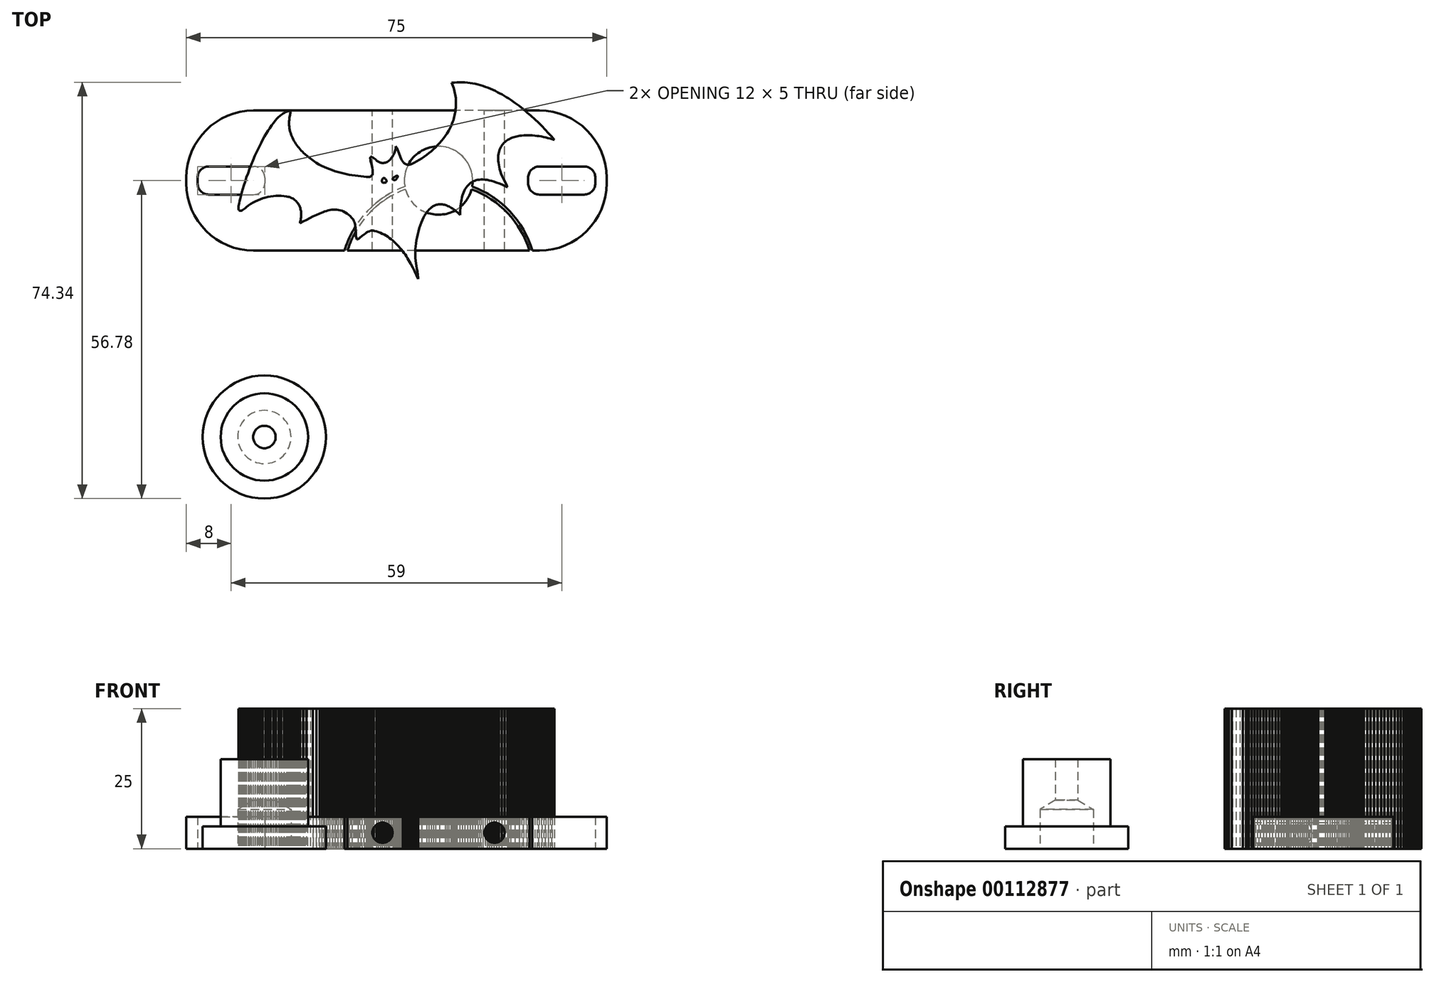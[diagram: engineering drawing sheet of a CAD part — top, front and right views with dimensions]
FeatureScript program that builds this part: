
annotation { "Feature Type Name" : "Feature", "Feature Type Description" : "" }
export const myFeature = defineFeature(function(context is Context, id is Id, definition is map)
    precondition{}
    {
        {
            var Q0;
            Q0=qCreatedBy(makeId("Top.planeOp"),FACE);
            var sketch = newSketch(context, id + "F0", { "sketchPlane" : qUnion([Q0])});
            skLineSegment(sketch, "E0.bottom", {"start": v(37.5, 12.5) * mm, "end": v(-37.5, 12.5) * mm});
            skLineSegment(sketch, "E0.top", {"start": v(37.5, -12.5) * mm, "end": v(24.27, -12.5) * mm});
            skLineSegment(sketch, "E0.left", {"start": v(37.5, 12.5) * mm, "end": v(37.5, -12.5) * mm});
            skLineSegment(sketch, "E0.right", {"start": v(-37.5, 12.5) * mm, "end": v(-37.5, -12.5) * mm});
            skPoint(sketch, "E0.middle", {"position": v(0, 0) * mm});
            skLineSegment(sketch, "E1", {"start": v(7.5, 12.5) * mm, "end": v(7.5, -12.5) * mm, "construction": true});
            skPoint(sketch, "E2", {"position": v(7.5, 0) * mm});
            skCircle(sketch, "E3", {"center": v(7.5, -17.5) * mm, "radius": 17.5 * mm});
            skCircle(sketch, "E4", {"center": v(7.5, -17.5) * mm, "radius": 17 * mm});
            skLineSegment(sketch, "E5.trimOffspring", {"start": v(-9.27, -12.5) * mm, "end": v(-37.5, -12.5) * mm});
            skLineSegment(sketch, "E6.trimOffspring", {"start": v(23.75, -12.5) * mm, "end": v(-8.75, -12.5) * mm});
            skLineSegment(sketch, "E7.bottom", {"start": v(35.5, 2.5) * mm, "end": v(23.5, 2.5) * mm});
            skLineSegment(sketch, "E7.top", {"start": v(35.5, -2.5) * mm, "end": v(23.5, -2.5) * mm});
            skLineSegment(sketch, "E7.left", {"start": v(35.5, 2.5) * mm, "end": v(35.5, -2.5) * mm});
            skLineSegment(sketch, "E7.right", {"start": v(23.5, 2.5) * mm, "end": v(23.5, -2.5) * mm});
            skPoint(sketch, "E7.middle", {"position": v(29.5, 0) * mm});
            skLineSegment(sketch, "E8.MirrorCS", {"start": v(-35.5, 2.5) * mm, "end": v(-23.5, 2.5) * mm});
            skLineSegment(sketch, "E9.MirrorCS", {"start": v(-23.5, 2.5) * mm, "end": v(-23.5, -2.5) * mm});
            skLineSegment(sketch, "E10.MirrorCS", {"start": v(-35.5, -2.5) * mm, "end": v(-23.5, -2.5) * mm});
            skLineSegment(sketch, "E11.MirrorCS", {"start": v(-35.5, 2.5) * mm, "end": v(-35.5, -2.5) * mm});
            skCircle(sketch, "E12", {"center": v(-23.58, -45.78) * mm, "radius": 11 * mm});
            skCircle(sketch, "E13", {"center": v(-23.58, -45.78) * mm, "radius": 7.8 * mm});
            skSolve(sketch);
        }
        {
            var Q0;
            Q0=makeQuery(id+"F0.imprint","IMPRINT",FACE,{"disambiguationData":[TD([[makeQuery(id+"F0.imprint","IMPRINT",EDGE,{"derivedFrom":sQuery(id+"F0.wireOp",EDGE,"E0.bottom")}),1.0]])]});
            extrude(context, id + "F1", {"entities" : qUnion([Q0]), "depth" : 5.7 * mm});
        }
        {
            var Q0;
            {var subQ0=sQuery(id+"F0.wireOp",EDGE,"E6.trimOffspring");Q0=makeQuery(id+"F0.imprint","IMPRINT",FACE,{"disambiguationData":[TD([[makeQuery(id+"F0.imprint","IMPRINT",EDGE,{"derivedFrom":subQ0}),-1.0]])]});}
            extrude(context, id + "F2", {"entities" : qUnion([Q0]), "depth" : 5.7 * mm});
        }
        {
            var Q0;
            Q0=makeQuery(id+"F1.opExtrude","SWEPT_FACE",FACE,{"disambiguationData":[OSD([sQuery(id+"F0.wireOp",EDGE,"E0.bottom")])]});
            var sketch = newSketch(context, id + "F3", { "sketchPlane" : qUnion([Q0])});
            skLineSegment(sketch, "E14", {"start": v(-7.5, 0) * mm, "end": v(-7.5, 5.7) * mm, "construction": true});
            skLineSegment(sketch, "E15", {"start": v(-37.5, 2.85) * mm, "end": v(37.5, 2.85) * mm, "construction": true});
            skPoint(sketch, "E16", {"position": v(2.5, 2.85) * mm});
            skPoint(sketch, "E17.MirrorP", {"position": v(-17.5, 2.85) * mm});
            skSolve(sketch);
        }
        {
            var Q0;
            Q0=sQuery(id+"F0.wireOp",VERTEX,"E2");
            var Q1;
            Q1=makeQuery(id+"F1.opExtrude","SWEPT_BODY",BODY,{"disambiguationData":[OSD([sQuery(id+"F0.wireOp",EDGE,"E0.bottom"),sQuery(id+"F0.wireOp",EDGE,"E0.top"),sQuery(id+"F0.wireOp",EDGE,"E0.left"),sQuery(id+"F0.wireOp",EDGE,"E0.right"),sQuery(id+"F0.wireOp",EDGE,"E3"),sQuery(id+"F0.wireOp",EDGE,"E5.trimOffspring"),sQuery(id+"F0.wireOp",EDGE,"E7.bottom"),sQuery(id+"F0.wireOp",EDGE,"E7.top"),sQuery(id+"F0.wireOp",EDGE,"E7.left"),sQuery(id+"F0.wireOp",EDGE,"E7.right"),sQuery(id+"F0.wireOp",EDGE,"E8.MirrorCS"),sQuery(id+"F0.wireOp",EDGE,"E9.MirrorCS"),sQuery(id+"F0.wireOp",EDGE,"E10.MirrorCS"),sQuery(id+"F0.wireOp",EDGE,"E11.MirrorCS")])]});
            var Q2;
            Q2=makeQuery(id+"F2.opExtrude","SWEPT_BODY",BODY,{"disambiguationData":[OSD([sQuery(id+"F0.wireOp",EDGE,"E4"),sQuery(id+"F0.wireOp",EDGE,"E6.trimOffspring")])]});
            hole(context, id + "F4", {"style" : HoleStyle.SIMPLE, "endStyle" : HoleEndStyle.THROUGH, "oppositeDirection" : true, "holeDiameter" : 12.2 * mm, "locations" : qUnion([Q0]), "scope" : qUnion([Q1, Q2]), "isTappedThrough" : true});
        }
        {
            var Q0;
            Q0=makeQuery(id+"F1.opExtrude","SWEPT_EDGE",EDGE,{"disambiguationData":[OSD([sQuery(id+"F0.wireOp",EDGE,"E0.bottom"),sQuery(id+"F0.wireOp",EDGE,"E0.right")])]});
            var Q1;
            Q1=makeQuery(id+"F1.opExtrude","SWEPT_EDGE",EDGE,{"disambiguationData":[OSD([sQuery(id+"F0.wireOp",EDGE,"E0.bottom"),sQuery(id+"F0.wireOp",EDGE,"E0.left")])]});
            var Q2;
            Q2=makeQuery(id+"F1.opExtrude","SWEPT_EDGE",EDGE,{"disambiguationData":[OSD([sQuery(id+"F0.wireOp",EDGE,"E0.right"),sQuery(id+"F0.wireOp",EDGE,"E5.trimOffspring")])]});
            var Q3;
            Q3=makeQuery(id+"F1.opExtrude","SWEPT_EDGE",EDGE,{"disambiguationData":[OSD([sQuery(id+"F0.wireOp",EDGE,"E0.top"),sQuery(id+"F0.wireOp",EDGE,"E0.left")])]});
            fillet(context, id + "F5", {"entities" : qUnion([Q0, Q1, Q2, Q3]), "radius" : 12 * mm, "tangentPropagation" : true, "allowEdgeOverflow" : false});
        }
        {
            var Q0;
            Q0=makeQuery(id+"F1.opExtrude","SWEPT_EDGE",EDGE,{"disambiguationData":[OSD([sQuery(id+"F0.wireOp",EDGE,"E7.bottom"),sQuery(id+"F0.wireOp",EDGE,"E7.right")])]});
            var Q1;
            Q1=makeQuery(id+"F1.opExtrude","SWEPT_EDGE",EDGE,{"disambiguationData":[OSD([sQuery(id+"F0.wireOp",EDGE,"E8.MirrorCS"),sQuery(id+"F0.wireOp",EDGE,"E11.MirrorCS")])]});
            var Q2;
            Q2=makeQuery(id+"F1.opExtrude","SWEPT_EDGE",EDGE,{"disambiguationData":[OSD([sQuery(id+"F0.wireOp",EDGE,"E8.MirrorCS"),sQuery(id+"F0.wireOp",EDGE,"E9.MirrorCS")])]});
            var Q3;
            Q3=makeQuery(id+"F1.opExtrude","SWEPT_EDGE",EDGE,{"disambiguationData":[OSD([sQuery(id+"F0.wireOp",EDGE,"E7.bottom"),sQuery(id+"F0.wireOp",EDGE,"E7.left")])]});
            var Q4;
            Q4=makeQuery(id+"F1.opExtrude","SWEPT_EDGE",EDGE,{"disambiguationData":[OSD([sQuery(id+"F0.wireOp",EDGE,"E7.top"),sQuery(id+"F0.wireOp",EDGE,"E7.left")])]});
            var Q5;
            Q5=makeQuery(id+"F1.opExtrude","SWEPT_EDGE",EDGE,{"disambiguationData":[OSD([sQuery(id+"F0.wireOp",EDGE,"E9.MirrorCS"),sQuery(id+"F0.wireOp",EDGE,"E10.MirrorCS")])]});
            var Q6;
            Q6=makeQuery(id+"F1.opExtrude","SWEPT_EDGE",EDGE,{"disambiguationData":[OSD([sQuery(id+"F0.wireOp",EDGE,"E10.MirrorCS"),sQuery(id+"F0.wireOp",EDGE,"E11.MirrorCS")])]});
            var Q7;
            Q7=makeQuery(id+"F1.opExtrude","SWEPT_EDGE",EDGE,{"disambiguationData":[OSD([sQuery(id+"F0.wireOp",EDGE,"E7.top"),sQuery(id+"F0.wireOp",EDGE,"E7.right")])]});
            fillet(context, id + "F6", {"entities" : qUnion([Q0, Q1, Q2, Q3, Q4, Q5, Q6, Q7]), "radius" : 2 * mm, "tangentPropagation" : true, "allowEdgeOverflow" : false});
        }
        {
            var Q0;
            Q0=sQuery(id+"F3.wireOp",VERTEX,"E17.MirrorP");
            var Q1;
            Q1=sQuery(id+"F3.wireOp",VERTEX,"E16");
            var Q2;
            Q2=makeQuery(id+"F1.opExtrude","SWEPT_BODY",BODY,{"disambiguationData":[OSD([sQuery(id+"F0.wireOp",EDGE,"E0.bottom"),sQuery(id+"F0.wireOp",EDGE,"E0.top"),sQuery(id+"F0.wireOp",EDGE,"E0.left"),sQuery(id+"F0.wireOp",EDGE,"E0.right"),sQuery(id+"F0.wireOp",EDGE,"E3"),sQuery(id+"F0.wireOp",EDGE,"E5.trimOffspring"),sQuery(id+"F0.wireOp",EDGE,"E7.bottom"),sQuery(id+"F0.wireOp",EDGE,"E7.top"),sQuery(id+"F0.wireOp",EDGE,"E7.left"),sQuery(id+"F0.wireOp",EDGE,"E7.right"),sQuery(id+"F0.wireOp",EDGE,"E8.MirrorCS"),sQuery(id+"F0.wireOp",EDGE,"E9.MirrorCS"),sQuery(id+"F0.wireOp",EDGE,"E10.MirrorCS"),sQuery(id+"F0.wireOp",EDGE,"E11.MirrorCS")])]});
            var Q3;
            Q3=makeQuery(id+"F2.opExtrude","SWEPT_BODY",BODY,{"disambiguationData":[OSD([sQuery(id+"F0.wireOp",EDGE,"E4"),sQuery(id+"F0.wireOp",EDGE,"E6.trimOffspring")])]});
            hole(context, id + "F7", {"style" : HoleStyle.SIMPLE, "endStyle" : HoleEndStyle.THROUGH, "holeDiameter" : 3.6 * mm, "locations" : qUnion([Q0, Q1]), "scope" : qUnion([Q2, Q3]), "isTappedThrough" : true});
        }
        {
            var Q0;
            Q0=makeQuery(id+"F0.imprint","IMPRINT",FACE,{"disambiguationData":[TD([[makeQuery(id+"F0.imprint","IMPRINT",EDGE,{"derivedFrom":sQuery(id+"F0.wireOp",EDGE,"E13")}),1.0]])]});
            extrude(context, id + "F8", {"entities" : qUnion([Q0]), "depth" : 16 * mm});
        }
        {
            var Q0;
            Q0=makeQuery(id+"F0.imprint","IMPRINT",FACE,{"disambiguationData":[TD([[makeQuery(id+"F0.imprint","IMPRINT",EDGE,{"derivedFrom":sQuery(id+"F0.wireOp",EDGE,"E12")}),1.0]])]});
            extrude(context, id + "F9", {"entities" : qUnion([Q0]), "operationType" : NewBodyOperationType.ADD, "depth" : 4 * mm});
        }
        {
            var Q0;
            Q0=sQuery(id+"F0.wireOp",VERTEX,"E12.center");
            var Q1;
            Q1=makeQuery(id+"F8.opExtrude","SWEPT_BODY",BODY,{"disambiguationData":[OSD([sQuery(id+"F0.wireOp",EDGE,"E13")])]});
            hole(context, id + "F10", {"style" : HoleStyle.SIMPLE, "endStyle" : HoleEndStyle.THROUGH, "oppositeDirection" : true, "holeDiameter" : 4 * mm, "locations" : qUnion([Q0]), "scope" : qUnion([Q1]), "isTappedThrough" : true});
        }
        {
            var Q0;
            Q0=sQuery(id+"F0.wireOp",VERTEX,"E12.center");
            var Q1;
            Q1=makeQuery(id+"F8.opExtrude","SWEPT_BODY",BODY,{"disambiguationData":[OSD([sQuery(id+"F0.wireOp",EDGE,"E13")])]});
            hole(context, id + "F11", {"style" : HoleStyle.SIMPLE, "endStyle" : HoleEndStyle.BLIND, "oppositeDirection" : true, "holeDiameter" : 9.5 * mm, "holeDepth" : 7 * mm, "locations" : qUnion([Q0]), "scope" : qUnion([Q1])});
        }
        {
            var Q0;
            Q0=qCreatedBy(makeId("Top.planeOp"),FACE);
            var sketch = newSketch(context, id + "F12", { "sketchPlane" : qUnion([Q0])});
            skLineSegment(sketch, "E18", {"start": v(3.84, -17.56) * mm, "end": v(3.55, -16.88) * mm});
            skLineSegment(sketch, "E19", {"start": v(3.55, -16.88) * mm, "end": v(3.24, -16.2) * mm});
            skLineSegment(sketch, "E20", {"start": v(3.24, -16.2) * mm, "end": v(2.9, -15.52) * mm});
            skLineSegment(sketch, "E21", {"start": v(2.9, -15.52) * mm, "end": v(2.56, -14.85) * mm});
            skLineSegment(sketch, "E22", {"start": v(2.56, -14.85) * mm, "end": v(2.18, -14.19) * mm});
            skLineSegment(sketch, "E23", {"start": v(2.18, -14.19) * mm, "end": v(1.98, -13.86) * mm});
            skLineSegment(sketch, "E24", {"start": v(1.98, -13.86) * mm, "end": v(1.78, -13.54) * mm});
            skLineSegment(sketch, "E25", {"start": v(1.78, -13.54) * mm, "end": v(1.57, -13.23) * mm});
            skLineSegment(sketch, "E26", {"start": v(1.57, -13.23) * mm, "end": v(1.35, -12.91) * mm});
            skLineSegment(sketch, "E27", {"start": v(1.35, -12.91) * mm, "end": v(1.12, -12.61) * mm});
            skLineSegment(sketch, "E28", {"start": v(1.12, -12.61) * mm, "end": v(0.9, -12.31) * mm});
            skLineSegment(sketch, "E29", {"start": v(0.9, -12.31) * mm, "end": v(0.65, -12.02) * mm});
            skLineSegment(sketch, "E30", {"start": v(0.65, -12.02) * mm, "end": v(0.4, -11.74) * mm});
            skLineSegment(sketch, "E31", {"start": v(0.4, -11.74) * mm, "end": v(0.15, -11.47) * mm});
            skLineSegment(sketch, "E32", {"start": v(0.15, -11.47) * mm, "end": v(-0.11, -11.2) * mm});
            skLineSegment(sketch, "E33", {"start": v(-0.11, -11.2) * mm, "end": v(-0.38, -10.95) * mm});
            skLineSegment(sketch, "E34", {"start": v(-0.38, -10.95) * mm, "end": v(-0.66, -10.7) * mm});
            skLineSegment(sketch, "E35", {"start": v(-0.66, -10.7) * mm, "end": v(-0.95, -10.47) * mm});
            skLineSegment(sketch, "E36", {"start": v(-0.95, -10.47) * mm, "end": v(-1.25, -10.25) * mm});
            skLineSegment(sketch, "E37", {"start": v(-1.25, -10.25) * mm, "end": v(-1.55, -10.04) * mm});
            skLineSegment(sketch, "E38", {"start": v(-1.55, -10.04) * mm, "end": v(-1.87, -9.85) * mm});
            skLineSegment(sketch, "E39", {"start": v(-1.87, -9.85) * mm, "end": v(-2.19, -9.67) * mm});
            skLineSegment(sketch, "E40", {"start": v(-2.19, -9.67) * mm, "end": v(-2.52, -9.5) * mm});
            skLineSegment(sketch, "E41", {"start": v(-2.52, -9.5) * mm, "end": v(-2.87, -9.35) * mm});
            skLineSegment(sketch, "E42", {"start": v(-2.87, -9.35) * mm, "end": v(-3.22, -9.2) * mm});
            skLineSegment(sketch, "E43", {"start": v(-3.22, -9.2) * mm, "end": v(-3.58, -9.09) * mm});
            skLineSegment(sketch, "E44", {"start": v(-3.58, -9.09) * mm, "end": v(-3.95, -8.98) * mm});
            skLineSegment(sketch, "E45", {"start": v(-3.95, -8.98) * mm, "end": v(-4.06, -8.95) * mm});
            skLineSegment(sketch, "E46", {"start": v(-4.06, -8.95) * mm, "end": v(-4.17, -8.93) * mm});
            skLineSegment(sketch, "E47", {"start": v(-4.17, -8.93) * mm, "end": v(-4.29, -8.93) * mm});
            skLineSegment(sketch, "E48", {"start": v(-4.29, -8.93) * mm, "end": v(-4.4, -8.93) * mm});
            skLineSegment(sketch, "E49", {"start": v(-4.4, -8.93) * mm, "end": v(-4.51, -8.95) * mm});
            skLineSegment(sketch, "E50", {"start": v(-4.51, -8.95) * mm, "end": v(-4.63, -8.97) * mm});
            skLineSegment(sketch, "E51", {"start": v(-4.63, -8.97) * mm, "end": v(-4.86, -9.05) * mm});
            skLineSegment(sketch, "E52", {"start": v(-4.86, -9.05) * mm, "end": v(-5.08, -9.15) * mm});
            skLineSegment(sketch, "E53", {"start": v(-5.08, -9.15) * mm, "end": v(-5.3, -9.28) * mm});
            skLineSegment(sketch, "E54", {"start": v(-5.3, -9.28) * mm, "end": v(-5.53, -9.43) * mm});
            skLineSegment(sketch, "E55", {"start": v(-5.53, -9.43) * mm, "end": v(-5.75, -9.58) * mm});
            skLineSegment(sketch, "E56", {"start": v(-5.75, -9.58) * mm, "end": v(-6.15, -9.9) * mm});
            skLineSegment(sketch, "E57", {"start": v(-6.15, -9.9) * mm, "end": v(-6.52, -10.2) * mm});
            skLineSegment(sketch, "E58", {"start": v(-6.52, -10.2) * mm, "end": v(-6.68, -10.33) * mm});
            skLineSegment(sketch, "E59", {"start": v(-6.68, -10.33) * mm, "end": v(-6.83, -10.43) * mm});
            skLineSegment(sketch, "E60", {"start": v(-6.83, -10.43) * mm, "end": v(-6.96, -10.5) * mm});
            skLineSegment(sketch, "E61", {"start": v(-6.96, -10.5) * mm, "end": v(-7.02, -10.53) * mm});
            skLineSegment(sketch, "E62", {"start": v(-7.02, -10.53) * mm, "end": v(-7.07, -10.54) * mm});
            skLineSegment(sketch, "E63", {"start": v(-7.07, -10.54) * mm, "end": v(-7.13, -10.34) * mm});
            skLineSegment(sketch, "E64", {"start": v(-7.13, -10.34) * mm, "end": v(-7.18, -10.14) * mm});
            skLineSegment(sketch, "E65", {"start": v(-7.18, -10.14) * mm, "end": v(-7.21, -9.93) * mm});
            skLineSegment(sketch, "E66", {"start": v(-7.21, -9.93) * mm, "end": v(-7.24, -9.72) * mm});
            skLineSegment(sketch, "E67", {"start": v(-7.24, -9.72) * mm, "end": v(-7.27, -9.27) * mm});
            skLineSegment(sketch, "E68", {"start": v(-7.27, -9.27) * mm, "end": v(-7.29, -8.82) * mm});
            skLineSegment(sketch, "E69", {"start": v(-7.29, -8.82) * mm, "end": v(-7.33, -8.35) * mm});
            skLineSegment(sketch, "E70", {"start": v(-7.33, -8.35) * mm, "end": v(-7.35, -8.12) * mm});
            skLineSegment(sketch, "E71", {"start": v(-7.35, -8.12) * mm, "end": v(-7.4, -7.89) * mm});
            skLineSegment(sketch, "E72", {"start": v(-7.4, -7.89) * mm, "end": v(-7.45, -7.66) * mm});
            skLineSegment(sketch, "E73", {"start": v(-7.45, -7.66) * mm, "end": v(-7.52, -7.43) * mm});
            skLineSegment(sketch, "E74", {"start": v(-7.52, -7.43) * mm, "end": v(-7.6, -7.2) * mm});
            skLineSegment(sketch, "E75", {"start": v(-7.6, -7.2) * mm, "end": v(-7.72, -6.98) * mm});
            skLineSegment(sketch, "E76", {"start": v(-7.72, -6.98) * mm, "end": v(-8, -6.64) * mm});
            skLineSegment(sketch, "E77", {"start": v(-8, -6.64) * mm, "end": v(-8.28, -6.35) * mm});
            skLineSegment(sketch, "E78", {"start": v(-8.28, -6.35) * mm, "end": v(-8.56, -6.09) * mm});
            skLineSegment(sketch, "E79", {"start": v(-8.56, -6.09) * mm, "end": v(-8.85, -5.86) * mm});
            skLineSegment(sketch, "E80", {"start": v(-8.85, -5.86) * mm, "end": v(-9.14, -5.68) * mm});
            skLineSegment(sketch, "E81", {"start": v(-9.14, -5.68) * mm, "end": v(-9.44, -5.52) * mm});
            skLineSegment(sketch, "E82", {"start": v(-9.44, -5.52) * mm, "end": v(-9.74, -5.4) * mm});
            skLineSegment(sketch, "E83", {"start": v(-9.74, -5.4) * mm, "end": v(-10.04, -5.3) * mm});
            skLineSegment(sketch, "E84", {"start": v(-10.04, -5.3) * mm, "end": v(-10.34, -5.24) * mm});
            skLineSegment(sketch, "E85", {"start": v(-10.34, -5.24) * mm, "end": v(-10.64, -5.2) * mm});
            skLineSegment(sketch, "E86", {"start": v(-10.64, -5.2) * mm, "end": v(-10.95, -5.18) * mm});
            skLineSegment(sketch, "E87", {"start": v(-10.95, -5.18) * mm, "end": v(-11.26, -5.2) * mm});
            skLineSegment(sketch, "E88", {"start": v(-11.26, -5.2) * mm, "end": v(-11.57, -5.22) * mm});
            skLineSegment(sketch, "E89", {"start": v(-11.57, -5.22) * mm, "end": v(-11.88, -5.27) * mm});
            skLineSegment(sketch, "E90", {"start": v(-11.88, -5.27) * mm, "end": v(-12.19, -5.34) * mm});
            skLineSegment(sketch, "E91", {"start": v(-12.19, -5.34) * mm, "end": v(-12.5, -5.42) * mm});
            skLineSegment(sketch, "E92", {"start": v(-12.5, -5.42) * mm, "end": v(-12.8, -5.52) * mm});
            skLineSegment(sketch, "E93", {"start": v(-12.8, -5.52) * mm, "end": v(-13.1, -5.62) * mm});
            skLineSegment(sketch, "E94", {"start": v(-13.1, -5.62) * mm, "end": v(-13.4, -5.74) * mm});
            skLineSegment(sketch, "E95", {"start": v(-13.4, -5.74) * mm, "end": v(-13.7, -5.86) * mm});
            skLineSegment(sketch, "E96", {"start": v(-13.7, -5.86) * mm, "end": v(-14.3, -6.14) * mm});
            skLineSegment(sketch, "E97", {"start": v(-14.3, -6.14) * mm, "end": v(-14.9, -6.43) * mm});
            skLineSegment(sketch, "E98", {"start": v(-14.9, -6.43) * mm, "end": v(-16.08, -7.04) * mm});
            skLineSegment(sketch, "E99", {"start": v(-16.08, -7.04) * mm, "end": v(-16.66, -7.32) * mm});
            skLineSegment(sketch, "E100", {"start": v(-16.66, -7.32) * mm, "end": v(-17.24, -7.58) * mm});
            skLineSegment(sketch, "E101", {"start": v(-17.24, -7.58) * mm, "end": v(-17.19, -7.4) * mm});
            skLineSegment(sketch, "E102", {"start": v(-17.19, -7.4) * mm, "end": v(-17.14, -7.2) * mm});
            skLineSegment(sketch, "E103", {"start": v(-17.14, -7.2) * mm, "end": v(-17.1, -7) * mm});
            skLineSegment(sketch, "E104", {"start": v(-17.1, -7) * mm, "end": v(-17.06, -6.81) * mm});
            skLineSegment(sketch, "E105", {"start": v(-17.06, -6.81) * mm, "end": v(-17.04, -6.62) * mm});
            skLineSegment(sketch, "E106", {"start": v(-17.04, -6.62) * mm, "end": v(-17.02, -6.43) * mm});
            skLineSegment(sketch, "E107", {"start": v(-17.02, -6.43) * mm, "end": v(-17, -6.23) * mm});
            skLineSegment(sketch, "E108", {"start": v(-17, -6.23) * mm, "end": v(-17, -6.04) * mm});
            skLineSegment(sketch, "E109", {"start": v(-17, -6.04) * mm, "end": v(-17.01, -5.85) * mm});
            skLineSegment(sketch, "E110", {"start": v(-17.01, -5.85) * mm, "end": v(-17.03, -5.66) * mm});
            skLineSegment(sketch, "E111", {"start": v(-17.03, -5.66) * mm, "end": v(-17.05, -5.48) * mm});
            skLineSegment(sketch, "E112", {"start": v(-17.05, -5.48) * mm, "end": v(-17.08, -5.3) * mm});
            skLineSegment(sketch, "E113", {"start": v(-17.08, -5.3) * mm, "end": v(-17.12, -5.12) * mm});
            skLineSegment(sketch, "E114", {"start": v(-17.12, -5.12) * mm, "end": v(-17.17, -4.94) * mm});
            skLineSegment(sketch, "E115", {"start": v(-17.17, -4.94) * mm, "end": v(-17.23, -4.77) * mm});
            skLineSegment(sketch, "E116", {"start": v(-17.23, -4.77) * mm, "end": v(-17.3, -4.6) * mm});
            skLineSegment(sketch, "E117", {"start": v(-17.3, -4.6) * mm, "end": v(-17.37, -4.44) * mm});
            skLineSegment(sketch, "E118", {"start": v(-17.37, -4.44) * mm, "end": v(-17.45, -4.28) * mm});
            skLineSegment(sketch, "E119", {"start": v(-17.45, -4.28) * mm, "end": v(-17.54, -4.13) * mm});
            skLineSegment(sketch, "E120", {"start": v(-17.54, -4.13) * mm, "end": v(-17.64, -3.98) * mm});
            skLineSegment(sketch, "E121", {"start": v(-17.64, -3.98) * mm, "end": v(-17.75, -3.84) * mm});
            skLineSegment(sketch, "E122", {"start": v(-17.75, -3.84) * mm, "end": v(-17.87, -3.7) * mm});
            skLineSegment(sketch, "E123", {"start": v(-17.87, -3.7) * mm, "end": v(-18, -3.58) * mm});
            skLineSegment(sketch, "E124", {"start": v(-18, -3.58) * mm, "end": v(-18.14, -3.46) * mm});
            skLineSegment(sketch, "E125", {"start": v(-18.14, -3.46) * mm, "end": v(-18.29, -3.35) * mm});
            skLineSegment(sketch, "E126", {"start": v(-18.29, -3.35) * mm, "end": v(-18.45, -3.25) * mm});
            skLineSegment(sketch, "E127", {"start": v(-18.45, -3.25) * mm, "end": v(-18.61, -3.16) * mm});
            skLineSegment(sketch, "E128", {"start": v(-18.61, -3.16) * mm, "end": v(-18.79, -3.07) * mm});
            skLineSegment(sketch, "E129", {"start": v(-18.79, -3.07) * mm, "end": v(-18.98, -3) * mm});
            skLineSegment(sketch, "E130", {"start": v(-18.98, -3) * mm, "end": v(-19.17, -2.93) * mm});
            skLineSegment(sketch, "E131", {"start": v(-19.17, -2.93) * mm, "end": v(-19.38, -2.88) * mm});
            skLineSegment(sketch, "E132", {"start": v(-19.38, -2.88) * mm, "end": v(-19.6, -2.84) * mm});
            skLineSegment(sketch, "E133", {"start": v(-19.6, -2.84) * mm, "end": v(-20.07, -2.78) * mm});
            skLineSegment(sketch, "E134", {"start": v(-20.07, -2.78) * mm, "end": v(-20.55, -2.74) * mm});
            skLineSegment(sketch, "E135", {"start": v(-20.55, -2.74) * mm, "end": v(-21.03, -2.73) * mm});
            skLineSegment(sketch, "E136", {"start": v(-21.03, -2.73) * mm, "end": v(-21.5, -2.75) * mm});
            skLineSegment(sketch, "E137", {"start": v(-21.5, -2.75) * mm, "end": v(-21.98, -2.79) * mm});
            skLineSegment(sketch, "E138", {"start": v(-21.98, -2.79) * mm, "end": v(-22.46, -2.85) * mm});
            skLineSegment(sketch, "E139", {"start": v(-22.46, -2.85) * mm, "end": v(-22.93, -2.94) * mm});
            skLineSegment(sketch, "E140", {"start": v(-22.93, -2.94) * mm, "end": v(-23.4, -3.05) * mm});
            skLineSegment(sketch, "E141", {"start": v(-23.4, -3.05) * mm, "end": v(-23.85, -3.19) * mm});
            skLineSegment(sketch, "E142", {"start": v(-23.85, -3.19) * mm, "end": v(-24.3, -3.34) * mm});
            skLineSegment(sketch, "E143", {"start": v(-24.3, -3.34) * mm, "end": v(-24.75, -3.53) * mm});
            skLineSegment(sketch, "E144", {"start": v(-24.75, -3.53) * mm, "end": v(-25.18, -3.73) * mm});
            skLineSegment(sketch, "E145", {"start": v(-25.18, -3.73) * mm, "end": v(-25.6, -3.95) * mm});
            skLineSegment(sketch, "E146", {"start": v(-25.6, -3.95) * mm, "end": v(-26.02, -4.2) * mm});
            skLineSegment(sketch, "E147", {"start": v(-26.02, -4.2) * mm, "end": v(-26.42, -4.46) * mm});
            skLineSegment(sketch, "E148", {"start": v(-26.42, -4.46) * mm, "end": v(-26.8, -4.75) * mm});
            skLineSegment(sketch, "E149", {"start": v(-26.8, -4.75) * mm, "end": v(-27, -4.93) * mm});
            skLineSegment(sketch, "E150", {"start": v(-27, -4.93) * mm, "end": v(-27.2, -5.09) * mm});
            skLineSegment(sketch, "E151", {"start": v(-27.2, -5.09) * mm, "end": v(-27.37, -5.2) * mm});
            skLineSegment(sketch, "E152", {"start": v(-27.37, -5.2) * mm, "end": v(-27.54, -5.3) * mm});
            skLineSegment(sketch, "E153", {"start": v(-27.54, -5.3) * mm, "end": v(-27.68, -5.37) * mm});
            skLineSegment(sketch, "E154", {"start": v(-27.68, -5.37) * mm, "end": v(-27.81, -5.4) * mm});
            skLineSegment(sketch, "E155", {"start": v(-27.81, -5.4) * mm, "end": v(-27.93, -5.4) * mm});
            skLineSegment(sketch, "E156", {"start": v(-27.93, -5.4) * mm, "end": v(-27.98, -5.4) * mm});
            skLineSegment(sketch, "E157", {"start": v(-27.98, -5.4) * mm, "end": v(-28.03, -5.37) * mm});
            skLineSegment(sketch, "E158", {"start": v(-28.03, -5.37) * mm, "end": v(-28.07, -5.35) * mm});
            skLineSegment(sketch, "E159", {"start": v(-28.07, -5.35) * mm, "end": v(-28.1, -5.32) * mm});
            skLineSegment(sketch, "E160", {"start": v(-28.1, -5.32) * mm, "end": v(-28.14, -5.28) * mm});
            skLineSegment(sketch, "E161", {"start": v(-28.14, -5.28) * mm, "end": v(-28.17, -5.23) * mm});
            skLineSegment(sketch, "E162", {"start": v(-28.17, -5.23) * mm, "end": v(-28.2, -5.1) * mm});
            skLineSegment(sketch, "E163", {"start": v(-28.2, -5.1) * mm, "end": v(-28.22, -4.96) * mm});
            skLineSegment(sketch, "E164", {"start": v(-28.22, -4.96) * mm, "end": v(-28.22, -4.78) * mm});
            skLineSegment(sketch, "E165", {"start": v(-28.22, -4.78) * mm, "end": v(-28.2, -4.57) * mm});
            skLineSegment(sketch, "E166", {"start": v(-28.2, -4.57) * mm, "end": v(-28.14, -4.33) * mm});
            skLineSegment(sketch, "E167", {"start": v(-28.14, -4.33) * mm, "end": v(-28.06, -4.05) * mm});
            skLineSegment(sketch, "E168", {"start": v(-28.06, -4.05) * mm, "end": v(-28, -3.66) * mm});
            skLineSegment(sketch, "E169", {"start": v(-28, -3.66) * mm, "end": v(-27.9, -3.2) * mm});
            skLineSegment(sketch, "E170", {"start": v(-27.9, -3.2) * mm, "end": v(-27.77, -2.7) * mm});
            skLineSegment(sketch, "E171", {"start": v(-27.77, -2.7) * mm, "end": v(-27.62, -2.13) * mm});
            skLineSegment(sketch, "E172", {"start": v(-27.62, -2.13) * mm, "end": v(-27.44, -1.51) * mm});
            skLineSegment(sketch, "E173", {"start": v(-27.44, -1.51) * mm, "end": v(-27.24, -0.85) * mm});
            skLineSegment(sketch, "E174", {"start": v(-27.24, -0.85) * mm, "end": v(-27.02, -0.16) * mm});
            skLineSegment(sketch, "E175", {"start": v(-27.02, -0.16) * mm, "end": v(-26.77, 0.56) * mm});
            skLineSegment(sketch, "E176", {"start": v(-26.77, 0.56) * mm, "end": v(-26.5, 1.31) * mm});
            skLineSegment(sketch, "E177", {"start": v(-26.5, 1.31) * mm, "end": v(-26.22, 2.08) * mm});
            skLineSegment(sketch, "E178", {"start": v(-26.22, 2.08) * mm, "end": v(-25.91, 2.86) * mm});
            skLineSegment(sketch, "E179", {"start": v(-25.91, 2.86) * mm, "end": v(-25.6, 3.65) * mm});
            skLineSegment(sketch, "E180", {"start": v(-25.6, 3.65) * mm, "end": v(-25.25, 4.43) * mm});
            skLineSegment(sketch, "E181", {"start": v(-25.25, 4.43) * mm, "end": v(-24.9, 5.22) * mm});
            skLineSegment(sketch, "E182", {"start": v(-24.9, 5.22) * mm, "end": v(-24.54, 5.99) * mm});
            skLineSegment(sketch, "E183", {"start": v(-24.54, 5.99) * mm, "end": v(-24.16, 6.75) * mm});
            skLineSegment(sketch, "E184", {"start": v(-24.16, 6.75) * mm, "end": v(-23.87, 7.3) * mm});
            skLineSegment(sketch, "E185", {"start": v(-23.87, 7.3) * mm, "end": v(-23.56, 7.86) * mm});
            skLineSegment(sketch, "E186", {"start": v(-23.56, 7.86) * mm, "end": v(-23.26, 8.38) * mm});
            skLineSegment(sketch, "E187", {"start": v(-23.26, 8.38) * mm, "end": v(-22.95, 8.9) * mm});
            skLineSegment(sketch, "E188", {"start": v(-22.95, 8.9) * mm, "end": v(-22.63, 9.38) * mm});
            skLineSegment(sketch, "E189", {"start": v(-22.63, 9.38) * mm, "end": v(-22.31, 9.84) * mm});
            skLineSegment(sketch, "E190", {"start": v(-22.31, 9.84) * mm, "end": v(-22, 10.27) * mm});
            skLineSegment(sketch, "E191", {"start": v(-22, 10.27) * mm, "end": v(-21.67, 10.67) * mm});
            skLineSegment(sketch, "E192", {"start": v(-21.67, 10.67) * mm, "end": v(-21.34, 11.03) * mm});
            skLineSegment(sketch, "E193", {"start": v(-21.34, 11.03) * mm, "end": v(-21.01, 11.36) * mm});
            skLineSegment(sketch, "E194", {"start": v(-21.01, 11.36) * mm, "end": v(-20.85, 11.51) * mm});
            skLineSegment(sketch, "E195", {"start": v(-20.85, 11.51) * mm, "end": v(-20.68, 11.65) * mm});
            skLineSegment(sketch, "E196", {"start": v(-20.68, 11.65) * mm, "end": v(-20.52, 11.78) * mm});
            skLineSegment(sketch, "E197", {"start": v(-20.52, 11.78) * mm, "end": v(-20.35, 11.9) * mm});
            skLineSegment(sketch, "E198", {"start": v(-20.35, 11.9) * mm, "end": v(-20.19, 12) * mm});
            skLineSegment(sketch, "E199", {"start": v(-20.19, 12) * mm, "end": v(-20.02, 12.1) * mm});
            skLineSegment(sketch, "E200", {"start": v(-20.02, 12.1) * mm, "end": v(-19.86, 12.2) * mm});
            skLineSegment(sketch, "E201", {"start": v(-19.86, 12.2) * mm, "end": v(-19.7, 12.26) * mm});
            skLineSegment(sketch, "E202", {"start": v(-19.7, 12.26) * mm, "end": v(-19.53, 12.33) * mm});
            skLineSegment(sketch, "E203", {"start": v(-19.53, 12.33) * mm, "end": v(-19.36, 12.37) * mm});
            skLineSegment(sketch, "E204", {"start": v(-19.36, 12.37) * mm, "end": v(-19.2, 12.41) * mm});
            skLineSegment(sketch, "E205", {"start": v(-19.2, 12.41) * mm, "end": v(-19.03, 12.43) * mm});
            skLineSegment(sketch, "E206", {"start": v(-19.03, 12.43) * mm, "end": v(-19, 12.4) * mm});
            skLineSegment(sketch, "E207", {"start": v(-19, 12.4) * mm, "end": v(-18.97, 12.36) * mm});
            skLineSegment(sketch, "E208", {"start": v(-18.97, 12.36) * mm, "end": v(-18.95, 12.31) * mm});
            skLineSegment(sketch, "E209", {"start": v(-18.95, 12.31) * mm, "end": v(-18.94, 12.25) * mm});
            skLineSegment(sketch, "E210", {"start": v(-18.94, 12.25) * mm, "end": v(-18.93, 12.17) * mm});
            skLineSegment(sketch, "E211", {"start": v(-18.93, 12.17) * mm, "end": v(-18.94, 12.08) * mm});
            skLineSegment(sketch, "E212", {"start": v(-18.94, 12.08) * mm, "end": v(-18.97, 11.86) * mm});
            skLineSegment(sketch, "E213", {"start": v(-18.97, 11.86) * mm, "end": v(-19.02, 11.7) * mm});
            skLineSegment(sketch, "E214", {"start": v(-19.02, 11.7) * mm, "end": v(-19.05, 11.54) * mm});
            skLineSegment(sketch, "E215", {"start": v(-19.05, 11.54) * mm, "end": v(-19.1, 11.22) * mm});
            skLineSegment(sketch, "E216", {"start": v(-19.1, 11.22) * mm, "end": v(-19.14, 10.9) * mm});
            skLineSegment(sketch, "E217", {"start": v(-19.14, 10.9) * mm, "end": v(-19.18, 10.56) * mm});
            skLineSegment(sketch, "E218", {"start": v(-19.18, 10.56) * mm, "end": v(-19.18, 10.24) * mm});
            skLineSegment(sketch, "E219", {"start": v(-19.18, 10.24) * mm, "end": v(-19.16, 9.93) * mm});
            skLineSegment(sketch, "E220", {"start": v(-19.16, 9.93) * mm, "end": v(-19.13, 9.62) * mm});
            skLineSegment(sketch, "E221", {"start": v(-19.13, 9.62) * mm, "end": v(-19.1, 9.32) * mm});
            skLineSegment(sketch, "E222", {"start": v(-19.1, 9.32) * mm, "end": v(-19.03, 9.02) * mm});
            skLineSegment(sketch, "E223", {"start": v(-19.03, 9.02) * mm, "end": v(-18.96, 8.73) * mm});
            skLineSegment(sketch, "E224", {"start": v(-18.96, 8.73) * mm, "end": v(-18.88, 8.44) * mm});
            skLineSegment(sketch, "E225", {"start": v(-18.88, 8.44) * mm, "end": v(-18.78, 8.15) * mm});
            skLineSegment(sketch, "E226", {"start": v(-18.78, 8.15) * mm, "end": v(-18.67, 7.88) * mm});
            skLineSegment(sketch, "E227", {"start": v(-18.67, 7.88) * mm, "end": v(-18.55, 7.6) * mm});
            skLineSegment(sketch, "E228", {"start": v(-18.55, 7.6) * mm, "end": v(-18.41, 7.33) * mm});
            skLineSegment(sketch, "E229", {"start": v(-18.41, 7.33) * mm, "end": v(-18.27, 7.07) * mm});
            skLineSegment(sketch, "E230", {"start": v(-18.27, 7.07) * mm, "end": v(-18.12, 6.81) * mm});
            skLineSegment(sketch, "E231", {"start": v(-18.12, 6.81) * mm, "end": v(-17.95, 6.56) * mm});
            skLineSegment(sketch, "E232", {"start": v(-17.95, 6.56) * mm, "end": v(-17.78, 6.31) * mm});
            skLineSegment(sketch, "E233", {"start": v(-17.78, 6.31) * mm, "end": v(-17.6, 6.07) * mm});
            skLineSegment(sketch, "E234", {"start": v(-17.6, 6.07) * mm, "end": v(-17.4, 5.83) * mm});
            skLineSegment(sketch, "E235", {"start": v(-17.4, 5.83) * mm, "end": v(-17.2, 5.6) * mm});
            skLineSegment(sketch, "E236", {"start": v(-17.2, 5.6) * mm, "end": v(-17, 5.37) * mm});
            skLineSegment(sketch, "E237", {"start": v(-17, 5.37) * mm, "end": v(-16.78, 5.15) * mm});
            skLineSegment(sketch, "E238", {"start": v(-16.78, 5.15) * mm, "end": v(-16.56, 4.93) * mm});
            skLineSegment(sketch, "E239", {"start": v(-16.56, 4.93) * mm, "end": v(-16.34, 4.72) * mm});
            skLineSegment(sketch, "E240", {"start": v(-16.34, 4.72) * mm, "end": v(-15.86, 4.3) * mm});
            skLineSegment(sketch, "E241", {"start": v(-15.86, 4.3) * mm, "end": v(-15.37, 3.92) * mm});
            skLineSegment(sketch, "E242", {"start": v(-15.37, 3.92) * mm, "end": v(-14.87, 3.56) * mm});
            skLineSegment(sketch, "E243", {"start": v(-14.87, 3.56) * mm, "end": v(-14.35, 3.21) * mm});
            skLineSegment(sketch, "E244", {"start": v(-14.35, 3.21) * mm, "end": v(-13.82, 2.89) * mm});
            skLineSegment(sketch, "E245", {"start": v(-13.82, 2.89) * mm, "end": v(-13.36, 2.65) * mm});
            skLineSegment(sketch, "E246", {"start": v(-13.36, 2.65) * mm, "end": v(-12.9, 2.42) * mm});
            skLineSegment(sketch, "E247", {"start": v(-12.9, 2.42) * mm, "end": v(-12.42, 2.2) * mm});
            skLineSegment(sketch, "E248", {"start": v(-12.42, 2.2) * mm, "end": v(-11.94, 2.02) * mm});
            skLineSegment(sketch, "E249", {"start": v(-11.94, 2.02) * mm, "end": v(-11.45, 1.84) * mm});
            skLineSegment(sketch, "E250", {"start": v(-11.45, 1.84) * mm, "end": v(-10.96, 1.67) * mm});
            skLineSegment(sketch, "E251", {"start": v(-10.96, 1.67) * mm, "end": v(-10.46, 1.52) * mm});
            skLineSegment(sketch, "E252", {"start": v(-10.46, 1.52) * mm, "end": v(-9.96, 1.38) * mm});
            skLineSegment(sketch, "E253", {"start": v(-9.96, 1.38) * mm, "end": v(-9.45, 1.26) * mm});
            skLineSegment(sketch, "E254", {"start": v(-9.45, 1.26) * mm, "end": v(-8.94, 1.15) * mm});
            skLineSegment(sketch, "E255", {"start": v(-8.94, 1.15) * mm, "end": v(-8.42, 1.04) * mm});
            skLineSegment(sketch, "E256", {"start": v(-8.42, 1.04) * mm, "end": v(-7.9, 0.96) * mm});
            skLineSegment(sketch, "E257", {"start": v(-7.9, 0.96) * mm, "end": v(-7.4, 0.88) * mm});
            skLineSegment(sketch, "E258", {"start": v(-7.4, 0.88) * mm, "end": v(-6.88, 0.8) * mm});
            skLineSegment(sketch, "E259", {"start": v(-6.88, 0.8) * mm, "end": v(-6.36, 0.75) * mm});
            skLineSegment(sketch, "E260", {"start": v(-6.36, 0.75) * mm, "end": v(-5.84, 0.7) * mm});
            skLineSegment(sketch, "E261", {"start": v(-5.84, 0.7) * mm, "end": v(-5.38, 0.65) * mm});
            skLineSegment(sketch, "E262", {"start": v(-5.38, 0.65) * mm, "end": v(-5.16, 0.63) * mm});
            skLineSegment(sketch, "E263", {"start": v(-5.16, 0.63) * mm, "end": v(-4.95, 0.63) * mm});
            skLineSegment(sketch, "E264", {"start": v(-4.95, 0.63) * mm, "end": v(-4.85, 0.65) * mm});
            skLineSegment(sketch, "E265", {"start": v(-4.85, 0.65) * mm, "end": v(-4.76, 0.67) * mm});
            skLineSegment(sketch, "E266", {"start": v(-4.76, 0.67) * mm, "end": v(-4.67, 0.7) * mm});
            skLineSegment(sketch, "E267", {"start": v(-4.67, 0.7) * mm, "end": v(-4.58, 0.75) * mm});
            skLineSegment(sketch, "E268", {"start": v(-4.58, 0.75) * mm, "end": v(-4.5, 0.81) * mm});
            skLineSegment(sketch, "E269", {"start": v(-4.5, 0.81) * mm, "end": v(-4.42, 0.89) * mm});
            skLineSegment(sketch, "E270", {"start": v(-4.42, 0.89) * mm, "end": v(-4.35, 0.98) * mm});
            skLineSegment(sketch, "E271", {"start": v(-4.35, 0.98) * mm, "end": v(-4.28, 1.1) * mm});
            skLineSegment(sketch, "E272", {"start": v(-4.28, 1.1) * mm, "end": v(-4.26, 1.21) * mm});
            skLineSegment(sketch, "E273", {"start": v(-4.26, 1.21) * mm, "end": v(-4.24, 1.34) * mm});
            skLineSegment(sketch, "E274", {"start": v(-4.24, 1.34) * mm, "end": v(-4.24, 1.49) * mm});
            skLineSegment(sketch, "E275", {"start": v(-4.24, 1.49) * mm, "end": v(-4.24, 1.63) * mm});
            skLineSegment(sketch, "E276", {"start": v(-4.24, 1.63) * mm, "end": v(-4.27, 1.95) * mm});
            skLineSegment(sketch, "E277", {"start": v(-4.27, 1.95) * mm, "end": v(-4.33, 2.27) * mm});
            skLineSegment(sketch, "E278", {"start": v(-4.33, 2.27) * mm, "end": v(-4.48, 2.93) * mm});
            skLineSegment(sketch, "E279", {"start": v(-4.48, 2.93) * mm, "end": v(-4.62, 3.53) * mm});
            skLineSegment(sketch, "E280", {"start": v(-4.62, 3.53) * mm, "end": v(-4.67, 3.78) * mm});
            skLineSegment(sketch, "E281", {"start": v(-4.67, 3.78) * mm, "end": v(-4.68, 3.99) * mm});
            skLineSegment(sketch, "E282", {"start": v(-4.68, 3.99) * mm, "end": v(-4.68, 4.07) * mm});
            skLineSegment(sketch, "E283", {"start": v(-4.68, 4.07) * mm, "end": v(-4.66, 4.14) * mm});
            skLineSegment(sketch, "E284", {"start": v(-4.66, 4.14) * mm, "end": v(-4.64, 4.2) * mm});
            skLineSegment(sketch, "E285", {"start": v(-4.64, 4.2) * mm, "end": v(-4.6, 4.23) * mm});
            skLineSegment(sketch, "E286", {"start": v(-4.6, 4.23) * mm, "end": v(-4.55, 4.25) * mm});
            skLineSegment(sketch, "E287", {"start": v(-4.55, 4.25) * mm, "end": v(-4.48, 4.24) * mm});
            skLineSegment(sketch, "E288", {"start": v(-4.48, 4.24) * mm, "end": v(-4.4, 4.22) * mm});
            skLineSegment(sketch, "E289", {"start": v(-4.4, 4.22) * mm, "end": v(-4.3, 4.17) * mm});
            skLineSegment(sketch, "E290", {"start": v(-4.3, 4.17) * mm, "end": v(-4.18, 4.1) * mm});
            skLineSegment(sketch, "E291", {"start": v(-4.18, 4.1) * mm, "end": v(-4.05, 4) * mm});
            skLineSegment(sketch, "E292", {"start": v(-4.05, 4) * mm, "end": v(-3.9, 3.88) * mm});
            skLineSegment(sketch, "E293", {"start": v(-3.9, 3.88) * mm, "end": v(-3.72, 3.74) * mm});
            skLineSegment(sketch, "E294", {"start": v(-3.72, 3.74) * mm, "end": v(-3.6, 3.63) * mm});
            skLineSegment(sketch, "E295", {"start": v(-3.6, 3.63) * mm, "end": v(-3.47, 3.53) * mm});
            skLineSegment(sketch, "E296", {"start": v(-3.47, 3.53) * mm, "end": v(-3.34, 3.44) * mm});
            skLineSegment(sketch, "E297", {"start": v(-3.34, 3.44) * mm, "end": v(-3.22, 3.37) * mm});
            skLineSegment(sketch, "E298", {"start": v(-3.22, 3.37) * mm, "end": v(-3.1, 3.3) * mm});
            skLineSegment(sketch, "E299", {"start": v(-3.1, 3.3) * mm, "end": v(-2.98, 3.25) * mm});
            skLineSegment(sketch, "E300", {"start": v(-2.98, 3.25) * mm, "end": v(-2.86, 3.2) * mm});
            skLineSegment(sketch, "E301", {"start": v(-2.86, 3.2) * mm, "end": v(-2.74, 3.18) * mm});
            skLineSegment(sketch, "E302", {"start": v(-2.74, 3.18) * mm, "end": v(-2.63, 3.15) * mm});
            skLineSegment(sketch, "E303", {"start": v(-2.63, 3.15) * mm, "end": v(-2.51, 3.14) * mm});
            skLineSegment(sketch, "E304", {"start": v(-2.51, 3.14) * mm, "end": v(-2.4, 3.14) * mm});
            skLineSegment(sketch, "E305", {"start": v(-2.4, 3.14) * mm, "end": v(-2.28, 3.14) * mm});
            skLineSegment(sketch, "E306", {"start": v(-2.28, 3.14) * mm, "end": v(-2.17, 3.16) * mm});
            skLineSegment(sketch, "E307", {"start": v(-2.17, 3.16) * mm, "end": v(-2.07, 3.18) * mm});
            skLineSegment(sketch, "E308", {"start": v(-2.07, 3.18) * mm, "end": v(-1.96, 3.21) * mm});
            skLineSegment(sketch, "E309", {"start": v(-1.96, 3.21) * mm, "end": v(-1.85, 3.25) * mm});
            skLineSegment(sketch, "E310", {"start": v(-1.85, 3.25) * mm, "end": v(-1.67, 3.34) * mm});
            skLineSegment(sketch, "E311", {"start": v(-1.67, 3.34) * mm, "end": v(-1.49, 3.45) * mm});
            skLineSegment(sketch, "E312", {"start": v(-1.49, 3.45) * mm, "end": v(-1.32, 3.57) * mm});
            skLineSegment(sketch, "E313", {"start": v(-1.32, 3.57) * mm, "end": v(-1.16, 3.72) * mm});
            skLineSegment(sketch, "E314", {"start": v(-1.16, 3.72) * mm, "end": v(-1, 3.88) * mm});
            skLineSegment(sketch, "E315", {"start": v(-1, 3.88) * mm, "end": v(-0.86, 4.06) * mm});
            skLineSegment(sketch, "E316", {"start": v(-0.86, 4.06) * mm, "end": v(-0.73, 4.24) * mm});
            skLineSegment(sketch, "E317", {"start": v(-0.73, 4.24) * mm, "end": v(-0.6, 4.44) * mm});
            skLineSegment(sketch, "E318", {"start": v(-0.6, 4.44) * mm, "end": v(-0.5, 4.64) * mm});
            skLineSegment(sketch, "E319", {"start": v(-0.5, 4.64) * mm, "end": v(-0.4, 4.85) * mm});
            skLineSegment(sketch, "E320", {"start": v(-0.4, 4.85) * mm, "end": v(-0.32, 5.06) * mm});
            skLineSegment(sketch, "E321", {"start": v(-0.32, 5.06) * mm, "end": v(-0.25, 5.28) * mm});
            skLineSegment(sketch, "E322", {"start": v(-0.25, 5.28) * mm, "end": v(-0.19, 5.49) * mm});
            skLineSegment(sketch, "E323", {"start": v(-0.19, 5.49) * mm, "end": v(-0.15, 5.7) * mm});
            skLineSegment(sketch, "E324", {"start": v(-0.15, 5.7) * mm, "end": v(-0.12, 5.9) * mm});
            skLineSegment(sketch, "E325", {"start": v(-0.12, 5.9) * mm, "end": v(-0.1, 6.1) * mm});
            skLineSegment(sketch, "E326", {"start": v(-0.1, 6.1) * mm, "end": v(0.05, 5.82) * mm});
            skLineSegment(sketch, "E327", {"start": v(0.05, 5.82) * mm, "end": v(0.19, 5.53) * mm});
            skLineSegment(sketch, "E328", {"start": v(0.19, 5.53) * mm, "end": v(0.44, 4.88) * mm});
            skLineSegment(sketch, "E329", {"start": v(0.44, 4.88) * mm, "end": v(0.7, 4.22) * mm});
            skLineSegment(sketch, "E330", {"start": v(0.7, 4.22) * mm, "end": v(0.83, 3.91) * mm});
            skLineSegment(sketch, "E331", {"start": v(0.83, 3.91) * mm, "end": v(0.97, 3.62) * mm});
            skLineSegment(sketch, "E332", {"start": v(0.97, 3.62) * mm, "end": v(1.11, 3.4) * mm});
            skLineSegment(sketch, "E333", {"start": v(1.11, 3.4) * mm, "end": v(1.19, 3.3) * mm});
            skLineSegment(sketch, "E334", {"start": v(1.19, 3.3) * mm, "end": v(1.27, 3.2) * mm});
            skLineSegment(sketch, "E335", {"start": v(1.27, 3.2) * mm, "end": v(1.35, 3.12) * mm});
            skLineSegment(sketch, "E336", {"start": v(1.35, 3.12) * mm, "end": v(1.44, 3.04) * mm});
            skLineSegment(sketch, "E337", {"start": v(1.44, 3.04) * mm, "end": v(1.53, 2.98) * mm});
            skLineSegment(sketch, "E338", {"start": v(1.53, 2.98) * mm, "end": v(1.63, 2.92) * mm});
            skLineSegment(sketch, "E339", {"start": v(1.63, 2.92) * mm, "end": v(1.73, 2.88) * mm});
            skLineSegment(sketch, "E340", {"start": v(1.73, 2.88) * mm, "end": v(1.84, 2.84) * mm});
            skLineSegment(sketch, "E341", {"start": v(1.84, 2.84) * mm, "end": v(1.96, 2.83) * mm});
            skLineSegment(sketch, "E342", {"start": v(1.96, 2.83) * mm, "end": v(2.09, 2.82) * mm});
            skLineSegment(sketch, "E343", {"start": v(2.09, 2.82) * mm, "end": v(2.22, 2.83) * mm});
            skLineSegment(sketch, "E344", {"start": v(2.22, 2.83) * mm, "end": v(2.36, 2.85) * mm});
            skLineSegment(sketch, "E345", {"start": v(2.36, 2.85) * mm, "end": v(2.5, 2.89) * mm});
            skLineSegment(sketch, "E346", {"start": v(2.5, 2.89) * mm, "end": v(2.66, 2.94) * mm});
            skLineSegment(sketch, "E347", {"start": v(2.66, 2.94) * mm, "end": v(3.15, 3.17) * mm});
            skLineSegment(sketch, "E348", {"start": v(3.15, 3.17) * mm, "end": v(3.62, 3.41) * mm});
            skLineSegment(sketch, "E349", {"start": v(3.62, 3.41) * mm, "end": v(4.08, 3.67) * mm});
            skLineSegment(sketch, "E350", {"start": v(4.08, 3.67) * mm, "end": v(4.53, 3.95) * mm});
            skLineSegment(sketch, "E351", {"start": v(4.53, 3.95) * mm, "end": v(4.97, 4.24) * mm});
            skLineSegment(sketch, "E352", {"start": v(4.97, 4.24) * mm, "end": v(5.4, 4.56) * mm});
            skLineSegment(sketch, "E353", {"start": v(5.4, 4.56) * mm, "end": v(5.8, 4.88) * mm});
            skLineSegment(sketch, "E354", {"start": v(5.8, 4.88) * mm, "end": v(6.2, 5.22) * mm});
            skLineSegment(sketch, "E355", {"start": v(6.2, 5.22) * mm, "end": v(6.6, 5.57) * mm});
            skLineSegment(sketch, "E356", {"start": v(6.6, 5.57) * mm, "end": v(6.97, 5.94) * mm});
            skLineSegment(sketch, "E357", {"start": v(6.97, 5.94) * mm, "end": v(7.33, 6.32) * mm});
            skLineSegment(sketch, "E358", {"start": v(7.33, 6.32) * mm, "end": v(7.69, 6.7) * mm});
            skLineSegment(sketch, "E359", {"start": v(7.69, 6.7) * mm, "end": v(8.03, 7.11) * mm});
            skLineSegment(sketch, "E360", {"start": v(8.03, 7.11) * mm, "end": v(8.37, 7.52) * mm});
            skLineSegment(sketch, "E361", {"start": v(8.37, 7.52) * mm, "end": v(8.7, 7.94) * mm});
            skLineSegment(sketch, "E362", {"start": v(8.7, 7.94) * mm, "end": v(9, 8.38) * mm});
            skLineSegment(sketch, "E363", {"start": v(9, 8.38) * mm, "end": v(9.3, 8.88) * mm});
            skLineSegment(sketch, "E364", {"start": v(9.3, 8.88) * mm, "end": v(9.57, 9.4) * mm});
            skLineSegment(sketch, "E365", {"start": v(9.57, 9.4) * mm, "end": v(9.7, 9.66) * mm});
            skLineSegment(sketch, "E366", {"start": v(9.7, 9.66) * mm, "end": v(9.82, 9.93) * mm});
            skLineSegment(sketch, "E367", {"start": v(9.82, 9.93) * mm, "end": v(9.93, 10.2) * mm});
            skLineSegment(sketch, "E368", {"start": v(9.93, 10.2) * mm, "end": v(10.03, 10.47) * mm});
            skLineSegment(sketch, "E369", {"start": v(10.03, 10.47) * mm, "end": v(10.13, 10.74) * mm});
            skLineSegment(sketch, "E370", {"start": v(10.13, 10.74) * mm, "end": v(10.21, 11.02) * mm});
            skLineSegment(sketch, "E371", {"start": v(10.21, 11.02) * mm, "end": v(10.3, 11.3) * mm});
            skLineSegment(sketch, "E372", {"start": v(10.3, 11.3) * mm, "end": v(10.37, 11.57) * mm});
            skLineSegment(sketch, "E373", {"start": v(10.37, 11.57) * mm, "end": v(10.43, 11.86) * mm});
            skLineSegment(sketch, "E374", {"start": v(10.43, 11.86) * mm, "end": v(10.48, 12.14) * mm});
            skLineSegment(sketch, "E375", {"start": v(10.48, 12.14) * mm, "end": v(10.53, 12.43) * mm});
            skLineSegment(sketch, "E376", {"start": v(10.53, 12.43) * mm, "end": v(10.57, 12.71) * mm});
            skLineSegment(sketch, "E377", {"start": v(10.57, 12.71) * mm, "end": v(10.6, 13) * mm});
            skLineSegment(sketch, "E378", {"start": v(10.6, 13) * mm, "end": v(10.62, 13.3) * mm});
            skLineSegment(sketch, "E379", {"start": v(10.62, 13.3) * mm, "end": v(10.63, 13.58) * mm});
            skLineSegment(sketch, "E380", {"start": v(10.63, 13.58) * mm, "end": v(10.63, 13.87) * mm});
            skLineSegment(sketch, "E381", {"start": v(10.63, 13.87) * mm, "end": v(10.62, 14.17) * mm});
            skLineSegment(sketch, "E382", {"start": v(10.62, 14.17) * mm, "end": v(10.6, 14.46) * mm});
            skLineSegment(sketch, "E383", {"start": v(10.6, 14.46) * mm, "end": v(10.58, 14.76) * mm});
            skLineSegment(sketch, "E384", {"start": v(10.58, 14.76) * mm, "end": v(10.54, 15.05) * mm});
            skLineSegment(sketch, "E385", {"start": v(10.54, 15.05) * mm, "end": v(10.5, 15.35) * mm});
            skLineSegment(sketch, "E386", {"start": v(10.5, 15.35) * mm, "end": v(10.44, 15.65) * mm});
            skLineSegment(sketch, "E387", {"start": v(10.44, 15.65) * mm, "end": v(10.37, 15.95) * mm});
            skLineSegment(sketch, "E388", {"start": v(10.37, 15.95) * mm, "end": v(10.29, 16.25) * mm});
            skLineSegment(sketch, "E389", {"start": v(10.29, 16.25) * mm, "end": v(10.2, 16.55) * mm});
            skLineSegment(sketch, "E390", {"start": v(10.2, 16.55) * mm, "end": v(10.1, 16.85) * mm});
            skLineSegment(sketch, "E391", {"start": v(10.1, 16.85) * mm, "end": v(10, 17.14) * mm});
            skLineSegment(sketch, "E392", {"start": v(10, 17.14) * mm, "end": v(9.87, 17.44) * mm});
            skLineSegment(sketch, "E393", {"start": v(9.87, 17.44) * mm, "end": v(10.34, 17.5) * mm});
            skLineSegment(sketch, "E394", {"start": v(10.34, 17.5) * mm, "end": v(10.8, 17.54) * mm});
            skLineSegment(sketch, "E395", {"start": v(10.8, 17.54) * mm, "end": v(11.28, 17.56) * mm});
            skLineSegment(sketch, "E396", {"start": v(11.28, 17.56) * mm, "end": v(11.74, 17.56) * mm});
            skLineSegment(sketch, "E397", {"start": v(11.74, 17.56) * mm, "end": v(12.2, 17.53) * mm});
            skLineSegment(sketch, "E398", {"start": v(12.2, 17.53) * mm, "end": v(12.67, 17.5) * mm});
            skLineSegment(sketch, "E399", {"start": v(12.67, 17.5) * mm, "end": v(13.14, 17.43) * mm});
            skLineSegment(sketch, "E400", {"start": v(13.14, 17.43) * mm, "end": v(13.6, 17.36) * mm});
            skLineSegment(sketch, "E401", {"start": v(13.6, 17.36) * mm, "end": v(14.06, 17.27) * mm});
            skLineSegment(sketch, "E402", {"start": v(14.06, 17.27) * mm, "end": v(14.52, 17.16) * mm});
            skLineSegment(sketch, "E403", {"start": v(14.52, 17.16) * mm, "end": v(14.98, 17.03) * mm});
            skLineSegment(sketch, "E404", {"start": v(14.98, 17.03) * mm, "end": v(15.43, 16.89) * mm});
            skLineSegment(sketch, "E405", {"start": v(15.43, 16.89) * mm, "end": v(15.88, 16.73) * mm});
            skLineSegment(sketch, "E406", {"start": v(15.88, 16.73) * mm, "end": v(16.33, 16.56) * mm});
            skLineSegment(sketch, "E407", {"start": v(16.33, 16.56) * mm, "end": v(16.78, 16.38) * mm});
            skLineSegment(sketch, "E408", {"start": v(16.78, 16.38) * mm, "end": v(17.23, 16.18) * mm});
            skLineSegment(sketch, "E409", {"start": v(17.23, 16.18) * mm, "end": v(17.63, 16) * mm});
            skLineSegment(sketch, "E410", {"start": v(17.63, 16) * mm, "end": v(18.03, 15.79) * mm});
            skLineSegment(sketch, "E411", {"start": v(18.03, 15.79) * mm, "end": v(18.43, 15.58) * mm});
            skLineSegment(sketch, "E412", {"start": v(18.43, 15.58) * mm, "end": v(18.83, 15.36) * mm});
            skLineSegment(sketch, "E413", {"start": v(18.83, 15.36) * mm, "end": v(19.22, 15.13) * mm});
            skLineSegment(sketch, "E414", {"start": v(19.22, 15.13) * mm, "end": v(19.61, 14.9) * mm});
            skLineSegment(sketch, "E415", {"start": v(19.61, 14.9) * mm, "end": v(20, 14.65) * mm});
            skLineSegment(sketch, "E416", {"start": v(20, 14.65) * mm, "end": v(20.38, 14.4) * mm});
            skLineSegment(sketch, "E417", {"start": v(20.38, 14.4) * mm, "end": v(21.14, 13.87) * mm});
            skLineSegment(sketch, "E418", {"start": v(21.14, 13.87) * mm, "end": v(21.88, 13.32) * mm});
            skLineSegment(sketch, "E419", {"start": v(21.88, 13.32) * mm, "end": v(22.6, 12.75) * mm});
            skLineSegment(sketch, "E420", {"start": v(22.6, 12.75) * mm, "end": v(23.31, 12.17) * mm});
            skLineSegment(sketch, "E421", {"start": v(23.31, 12.17) * mm, "end": v(24, 11.56) * mm});
            skLineSegment(sketch, "E422", {"start": v(24, 11.56) * mm, "end": v(24.67, 10.95) * mm});
            skLineSegment(sketch, "E423", {"start": v(24.67, 10.95) * mm, "end": v(25.32, 10.33) * mm});
            skLineSegment(sketch, "E424", {"start": v(25.32, 10.33) * mm, "end": v(25.95, 9.71) * mm});
            skLineSegment(sketch, "E425", {"start": v(25.95, 9.71) * mm, "end": v(26.55, 9.09) * mm});
            skLineSegment(sketch, "E426", {"start": v(26.55, 9.09) * mm, "end": v(27.13, 8.47) * mm});
            skLineSegment(sketch, "E427", {"start": v(27.13, 8.47) * mm, "end": v(27.7, 7.86) * mm});
            skLineSegment(sketch, "E428", {"start": v(27.7, 7.86) * mm, "end": v(28.22, 7.26) * mm});
            skLineSegment(sketch, "E429", {"start": v(28.22, 7.26) * mm, "end": v(27.84, 7.38) * mm});
            skLineSegment(sketch, "E430", {"start": v(27.84, 7.38) * mm, "end": v(27.45, 7.5) * mm});
            skLineSegment(sketch, "E431", {"start": v(27.45, 7.5) * mm, "end": v(27.06, 7.6) * mm});
            skLineSegment(sketch, "E432", {"start": v(27.06, 7.6) * mm, "end": v(26.66, 7.7) * mm});
            skLineSegment(sketch, "E433", {"start": v(26.66, 7.7) * mm, "end": v(26.26, 7.78) * mm});
            skLineSegment(sketch, "E434", {"start": v(26.26, 7.78) * mm, "end": v(25.87, 7.85) * mm});
            skLineSegment(sketch, "E435", {"start": v(25.87, 7.85) * mm, "end": v(25.46, 7.92) * mm});
            skLineSegment(sketch, "E436", {"start": v(25.46, 7.92) * mm, "end": v(25.07, 7.98) * mm});
            skLineSegment(sketch, "E437", {"start": v(25.07, 7.98) * mm, "end": v(24.67, 8.02) * mm});
            skLineSegment(sketch, "E438", {"start": v(24.67, 8.02) * mm, "end": v(24.27, 8.06) * mm});
            skLineSegment(sketch, "E439", {"start": v(24.27, 8.06) * mm, "end": v(23.88, 8.08) * mm});
            skLineSegment(sketch, "E440", {"start": v(23.88, 8.08) * mm, "end": v(23.5, 8.09) * mm});
            skLineSegment(sketch, "E441", {"start": v(23.5, 8.09) * mm, "end": v(23.11, 8.08) * mm});
            skLineSegment(sketch, "E442", {"start": v(23.11, 8.08) * mm, "end": v(22.74, 8.06) * mm});
            skLineSegment(sketch, "E443", {"start": v(22.74, 8.06) * mm, "end": v(22.37, 8.03) * mm});
            skLineSegment(sketch, "E444", {"start": v(22.37, 8.03) * mm, "end": v(22.01, 7.99) * mm});
            skLineSegment(sketch, "E445", {"start": v(22.01, 7.99) * mm, "end": v(21.75, 7.95) * mm});
            skLineSegment(sketch, "E446", {"start": v(21.75, 7.95) * mm, "end": v(21.5, 7.9) * mm});
            skLineSegment(sketch, "E447", {"start": v(21.5, 7.9) * mm, "end": v(21.25, 7.84) * mm});
            skLineSegment(sketch, "E448", {"start": v(21.25, 7.84) * mm, "end": v(21.01, 7.77) * mm});
            skLineSegment(sketch, "E449", {"start": v(21.01, 7.77) * mm, "end": v(20.78, 7.7) * mm});
            skLineSegment(sketch, "E450", {"start": v(20.78, 7.7) * mm, "end": v(20.55, 7.6) * mm});
            skLineSegment(sketch, "E451", {"start": v(20.55, 7.6) * mm, "end": v(20.33, 7.51) * mm});
            skLineSegment(sketch, "E452", {"start": v(20.33, 7.51) * mm, "end": v(20.12, 7.4) * mm});
            skLineSegment(sketch, "E453", {"start": v(20.12, 7.4) * mm, "end": v(19.92, 7.3) * mm});
            skLineSegment(sketch, "E454", {"start": v(19.92, 7.3) * mm, "end": v(19.73, 7.17) * mm});
            skLineSegment(sketch, "E455", {"start": v(19.73, 7.17) * mm, "end": v(19.54, 7.04) * mm});
            skLineSegment(sketch, "E456", {"start": v(19.54, 7.04) * mm, "end": v(19.37, 6.9) * mm});
            skLineSegment(sketch, "E457", {"start": v(19.37, 6.9) * mm, "end": v(19.2, 6.75) * mm});
            skLineSegment(sketch, "E458", {"start": v(19.2, 6.75) * mm, "end": v(19.05, 6.58) * mm});
            skLineSegment(sketch, "E459", {"start": v(19.05, 6.58) * mm, "end": v(18.9, 6.41) * mm});
            skLineSegment(sketch, "E460", {"start": v(18.9, 6.41) * mm, "end": v(18.77, 6.23) * mm});
            skLineSegment(sketch, "E461", {"start": v(18.77, 6.23) * mm, "end": v(18.64, 6.02) * mm});
            skLineSegment(sketch, "E462", {"start": v(18.64, 6.02) * mm, "end": v(18.53, 5.8) * mm});
            skLineSegment(sketch, "E463", {"start": v(18.53, 5.8) * mm, "end": v(18.43, 5.56) * mm});
            skLineSegment(sketch, "E464", {"start": v(18.43, 5.56) * mm, "end": v(18.34, 5.3) * mm});
            skLineSegment(sketch, "E465", {"start": v(18.34, 5.3) * mm, "end": v(18.27, 5.05) * mm});
            skLineSegment(sketch, "E466", {"start": v(18.27, 5.05) * mm, "end": v(18.22, 4.77) * mm});
            skLineSegment(sketch, "E467", {"start": v(18.22, 4.77) * mm, "end": v(18.18, 4.48) * mm});
            skLineSegment(sketch, "E468", {"start": v(18.18, 4.48) * mm, "end": v(18.16, 4.18) * mm});
            skLineSegment(sketch, "E469", {"start": v(18.16, 4.18) * mm, "end": v(18.16, 3.86) * mm});
            skLineSegment(sketch, "E470", {"start": v(18.16, 3.86) * mm, "end": v(18.17, 3.53) * mm});
            skLineSegment(sketch, "E471", {"start": v(18.17, 3.53) * mm, "end": v(18.2, 3.18) * mm});
            skLineSegment(sketch, "E472", {"start": v(18.2, 3.18) * mm, "end": v(18.25, 2.82) * mm});
            skLineSegment(sketch, "E473", {"start": v(18.25, 2.82) * mm, "end": v(18.32, 2.44) * mm});
            skLineSegment(sketch, "E474", {"start": v(18.32, 2.44) * mm, "end": v(18.42, 2.04) * mm});
            skLineSegment(sketch, "E475", {"start": v(18.42, 2.04) * mm, "end": v(18.53, 1.63) * mm});
            skLineSegment(sketch, "E476", {"start": v(18.53, 1.63) * mm, "end": v(18.66, 1.2) * mm});
            skLineSegment(sketch, "E477", {"start": v(18.66, 1.2) * mm, "end": v(18.85, 0.77) * mm});
            skLineSegment(sketch, "E478", {"start": v(18.85, 0.77) * mm, "end": v(19.04, 0.37) * mm});
            skLineSegment(sketch, "E479", {"start": v(19.04, 0.37) * mm, "end": v(19.4, -0.34) * mm});
            skLineSegment(sketch, "E480", {"start": v(19.4, -0.34) * mm, "end": v(19.67, -0.86) * mm});
            skLineSegment(sketch, "E481", {"start": v(19.67, -0.86) * mm, "end": v(19.75, -1.05) * mm});
            skLineSegment(sketch, "E482", {"start": v(19.75, -1.05) * mm, "end": v(19.78, -1.12) * mm});
            skLineSegment(sketch, "E483", {"start": v(19.78, -1.12) * mm, "end": v(19.79, -1.17) * mm});
            skLineSegment(sketch, "E484", {"start": v(19.79, -1.17) * mm, "end": v(19.27, -0.93) * mm});
            skLineSegment(sketch, "E485", {"start": v(19.27, -0.93) * mm, "end": v(18.78, -0.71) * mm});
            skLineSegment(sketch, "E486", {"start": v(18.78, -0.71) * mm, "end": v(18.3, -0.52) * mm});
            skLineSegment(sketch, "E487", {"start": v(18.3, -0.52) * mm, "end": v(17.83, -0.34) * mm});
            skLineSegment(sketch, "E488", {"start": v(17.83, -0.34) * mm, "end": v(17.4, -0.19) * mm});
            skLineSegment(sketch, "E489", {"start": v(17.4, -0.19) * mm, "end": v(16.97, -0.06) * mm});
            skLineSegment(sketch, "E490", {"start": v(16.97, -0.06) * mm, "end": v(16.56, 0.04) * mm});
            skLineSegment(sketch, "E491", {"start": v(16.56, 0.04) * mm, "end": v(16.18, 0.12) * mm});
            skLineSegment(sketch, "E492", {"start": v(16.18, 0.12) * mm, "end": v(15.8, 0.17) * mm});
            skLineSegment(sketch, "E493", {"start": v(15.8, 0.17) * mm, "end": v(15.46, 0.2) * mm});
            skLineSegment(sketch, "E494", {"start": v(15.46, 0.2) * mm, "end": v(15.12, 0.2) * mm});
            skLineSegment(sketch, "E495", {"start": v(15.12, 0.2) * mm, "end": v(14.8, 0.17) * mm});
            skLineSegment(sketch, "E496", {"start": v(14.8, 0.17) * mm, "end": v(14.5, 0.12) * mm});
            skLineSegment(sketch, "E497", {"start": v(14.5, 0.12) * mm, "end": v(14.21, 0.05) * mm});
            skLineSegment(sketch, "E498", {"start": v(14.21, 0.05) * mm, "end": v(13.94, -0.04) * mm});
            skLineSegment(sketch, "E499", {"start": v(13.94, -0.04) * mm, "end": v(13.69, -0.15) * mm});
            skLineSegment(sketch, "E500", {"start": v(13.69, -0.15) * mm, "end": v(13.45, -0.28) * mm});
            skLineSegment(sketch, "E501", {"start": v(13.45, -0.28) * mm, "end": v(13.22, -0.43) * mm});
            skLineSegment(sketch, "E502", {"start": v(13.22, -0.43) * mm, "end": v(13.01, -0.6) * mm});
            skLineSegment(sketch, "E503", {"start": v(13.01, -0.6) * mm, "end": v(12.81, -0.79) * mm});
            skLineSegment(sketch, "E504", {"start": v(12.81, -0.79) * mm, "end": v(12.62, -1) * mm});
            skLineSegment(sketch, "E505", {"start": v(12.62, -1) * mm, "end": v(12.44, -1.24) * mm});
            skLineSegment(sketch, "E506", {"start": v(12.44, -1.24) * mm, "end": v(12.28, -1.5) * mm});
            skLineSegment(sketch, "E507", {"start": v(12.28, -1.5) * mm, "end": v(12.13, -1.78) * mm});
            skLineSegment(sketch, "E508", {"start": v(12.13, -1.78) * mm, "end": v(12, -2.07) * mm});
            skLineSegment(sketch, "E509", {"start": v(12, -2.07) * mm, "end": v(11.88, -2.38) * mm});
            skLineSegment(sketch, "E510", {"start": v(11.88, -2.38) * mm, "end": v(11.77, -2.7) * mm});
            skLineSegment(sketch, "E511", {"start": v(11.77, -2.7) * mm, "end": v(11.68, -3.04) * mm});
            skLineSegment(sketch, "E512", {"start": v(11.68, -3.04) * mm, "end": v(11.6, -3.39) * mm});
            skLineSegment(sketch, "E513", {"start": v(11.6, -3.39) * mm, "end": v(11.54, -3.75) * mm});
            skLineSegment(sketch, "E514", {"start": v(11.54, -3.75) * mm, "end": v(11.48, -4.13) * mm});
            skLineSegment(sketch, "E515", {"start": v(11.48, -4.13) * mm, "end": v(11.44, -4.51) * mm});
            skLineSegment(sketch, "E516", {"start": v(11.44, -4.51) * mm, "end": v(11.41, -4.91) * mm});
            skLineSegment(sketch, "E517", {"start": v(11.41, -4.91) * mm, "end": v(11.4, -5.32) * mm});
            skLineSegment(sketch, "E518", {"start": v(11.4, -5.32) * mm, "end": v(11.39, -5.74) * mm});
            skLineSegment(sketch, "E519", {"start": v(11.39, -5.74) * mm, "end": v(11.4, -6.16) * mm});
            skLineSegment(sketch, "E520", {"start": v(11.4, -6.16) * mm, "end": v(11.15, -5.93) * mm});
            skLineSegment(sketch, "E521", {"start": v(11.15, -5.93) * mm, "end": v(10.91, -5.71) * mm});
            skLineSegment(sketch, "E522", {"start": v(10.91, -5.71) * mm, "end": v(10.68, -5.51) * mm});
            skLineSegment(sketch, "E523", {"start": v(10.68, -5.51) * mm, "end": v(10.45, -5.33) * mm});
            skLineSegment(sketch, "E524", {"start": v(10.45, -5.33) * mm, "end": v(10.23, -5.16) * mm});
            skLineSegment(sketch, "E525", {"start": v(10.23, -5.16) * mm, "end": v(10, -5) * mm});
            skLineSegment(sketch, "E526", {"start": v(10, -5) * mm, "end": v(9.8, -4.86) * mm});
            skLineSegment(sketch, "E527", {"start": v(9.8, -4.86) * mm, "end": v(9.58, -4.74) * mm});
            skLineSegment(sketch, "E528", {"start": v(9.58, -4.74) * mm, "end": v(9.37, -4.63) * mm});
            skLineSegment(sketch, "E529", {"start": v(9.37, -4.63) * mm, "end": v(9.17, -4.54) * mm});
            skLineSegment(sketch, "E530", {"start": v(9.17, -4.54) * mm, "end": v(8.96, -4.45) * mm});
            skLineSegment(sketch, "E531", {"start": v(8.96, -4.45) * mm, "end": v(8.77, -4.39) * mm});
            skLineSegment(sketch, "E532", {"start": v(8.77, -4.39) * mm, "end": v(8.58, -4.33) * mm});
            skLineSegment(sketch, "E533", {"start": v(8.58, -4.33) * mm, "end": v(8.39, -4.29) * mm});
            skLineSegment(sketch, "E534", {"start": v(8.39, -4.29) * mm, "end": v(8.2, -4.26) * mm});
            skLineSegment(sketch, "E535", {"start": v(8.2, -4.26) * mm, "end": v(8.02, -4.24) * mm});
            skLineSegment(sketch, "E536", {"start": v(8.02, -4.24) * mm, "end": v(7.84, -4.23) * mm});
            skLineSegment(sketch, "E537", {"start": v(7.84, -4.23) * mm, "end": v(7.67, -4.24) * mm});
            skLineSegment(sketch, "E538", {"start": v(7.67, -4.24) * mm, "end": v(7.5, -4.26) * mm});
            skLineSegment(sketch, "E539", {"start": v(7.5, -4.26) * mm, "end": v(7.33, -4.29) * mm});
            skLineSegment(sketch, "E540", {"start": v(7.33, -4.29) * mm, "end": v(7.17, -4.33) * mm});
            skLineSegment(sketch, "E541", {"start": v(7.17, -4.33) * mm, "end": v(7.01, -4.38) * mm});
            skLineSegment(sketch, "E542", {"start": v(7.01, -4.38) * mm, "end": v(6.86, -4.44) * mm});
            skLineSegment(sketch, "E543", {"start": v(6.86, -4.44) * mm, "end": v(6.7, -4.5) * mm});
            skLineSegment(sketch, "E544", {"start": v(6.7, -4.5) * mm, "end": v(6.56, -4.59) * mm});
            skLineSegment(sketch, "E545", {"start": v(6.56, -4.59) * mm, "end": v(6.41, -4.68) * mm});
            skLineSegment(sketch, "E546", {"start": v(6.41, -4.68) * mm, "end": v(6.27, -4.77) * mm});
            skLineSegment(sketch, "E547", {"start": v(6.27, -4.77) * mm, "end": v(6.14, -4.88) * mm});
            skLineSegment(sketch, "E548", {"start": v(6.14, -4.88) * mm, "end": v(6, -5) * mm});
            skLineSegment(sketch, "E549", {"start": v(6, -5) * mm, "end": v(5.87, -5.12) * mm});
            skLineSegment(sketch, "E550", {"start": v(5.87, -5.12) * mm, "end": v(5.62, -5.39) * mm});
            skLineSegment(sketch, "E551", {"start": v(5.62, -5.39) * mm, "end": v(5.48, -5.56) * mm});
            skLineSegment(sketch, "E552", {"start": v(5.48, -5.56) * mm, "end": v(5.34, -5.74) * mm});
            skLineSegment(sketch, "E553", {"start": v(5.34, -5.74) * mm, "end": v(5.21, -5.94) * mm});
            skLineSegment(sketch, "E554", {"start": v(5.21, -5.94) * mm, "end": v(5.08, -6.14) * mm});
            skLineSegment(sketch, "E555", {"start": v(5.08, -6.14) * mm, "end": v(4.96, -6.35) * mm});
            skLineSegment(sketch, "E556", {"start": v(4.96, -6.35) * mm, "end": v(4.84, -6.57) * mm});
            skLineSegment(sketch, "E557", {"start": v(4.84, -6.57) * mm, "end": v(4.62, -7.02) * mm});
            skLineSegment(sketch, "E558", {"start": v(4.62, -7.02) * mm, "end": v(4.42, -7.5) * mm});
            skLineSegment(sketch, "E559", {"start": v(4.42, -7.5) * mm, "end": v(4.24, -8) * mm});
            skLineSegment(sketch, "E560", {"start": v(4.24, -8) * mm, "end": v(4.07, -8.52) * mm});
            skLineSegment(sketch, "E561", {"start": v(4.07, -8.52) * mm, "end": v(3.92, -9.05) * mm});
            skLineSegment(sketch, "E562", {"start": v(3.92, -9.05) * mm, "end": v(3.8, -9.6) * mm});
            skLineSegment(sketch, "E563", {"start": v(3.8, -9.6) * mm, "end": v(3.68, -10.13) * mm});
            skLineSegment(sketch, "E564", {"start": v(3.68, -10.13) * mm, "end": v(3.58, -10.68) * mm});
            skLineSegment(sketch, "E565", {"start": v(3.58, -10.68) * mm, "end": v(3.5, -11.22) * mm});
            skLineSegment(sketch, "E566", {"start": v(3.5, -11.22) * mm, "end": v(3.44, -11.75) * mm});
            skLineSegment(sketch, "E567", {"start": v(3.44, -11.75) * mm, "end": v(3.4, -12.26) * mm});
            skLineSegment(sketch, "E568", {"start": v(3.4, -12.26) * mm, "end": v(3.36, -12.77) * mm});
            skLineSegment(sketch, "E569", {"start": v(3.36, -12.77) * mm, "end": v(3.35, -13.25) * mm});
            skLineSegment(sketch, "E570", {"start": v(3.35, -13.25) * mm, "end": v(3.35, -13.5) * mm});
            skLineSegment(sketch, "E571", {"start": v(3.35, -13.5) * mm, "end": v(3.37, -13.76) * mm});
            skLineSegment(sketch, "E572", {"start": v(3.37, -13.76) * mm, "end": v(3.44, -14.36) * mm});
            skLineSegment(sketch, "E573", {"start": v(3.44, -14.36) * mm, "end": v(3.63, -15.66) * mm});
            skLineSegment(sketch, "E574", {"start": v(3.63, -15.66) * mm, "end": v(3.72, -16.27) * mm});
            skLineSegment(sketch, "E575", {"start": v(3.72, -16.27) * mm, "end": v(3.8, -16.82) * mm});
            skLineSegment(sketch, "E576", {"start": v(3.8, -16.82) * mm, "end": v(3.83, -17.06) * mm});
            skLineSegment(sketch, "E577", {"start": v(3.83, -17.06) * mm, "end": v(3.85, -17.26) * mm});
            skLineSegment(sketch, "E578", {"start": v(3.85, -17.26) * mm, "end": v(3.85, -17.43) * mm});
            skLineSegment(sketch, "E579", {"start": v(3.85, -17.43) * mm, "end": v(3.84, -17.56) * mm});
            skLineSegment(sketch, "E580", {"start": v(-2.22, 0.47) * mm, "end": v(-2.28, 0.46) * mm});
            skLineSegment(sketch, "E581", {"start": v(-2.28, 0.46) * mm, "end": v(-2.34, 0.44) * mm});
            skLineSegment(sketch, "E582", {"start": v(-2.34, 0.44) * mm, "end": v(-2.4, 0.4) * mm});
            skLineSegment(sketch, "E583", {"start": v(-2.4, 0.4) * mm, "end": v(-2.44, 0.36) * mm});
            skLineSegment(sketch, "E584", {"start": v(-2.44, 0.36) * mm, "end": v(-2.48, 0.3) * mm});
            skLineSegment(sketch, "E585", {"start": v(-2.48, 0.3) * mm, "end": v(-2.52, 0.24) * mm});
            skLineSegment(sketch, "E586", {"start": v(-2.52, 0.24) * mm, "end": v(-2.55, 0.18) * mm});
            skLineSegment(sketch, "E587", {"start": v(-2.55, 0.18) * mm, "end": v(-2.57, 0.1) * mm});
            skLineSegment(sketch, "E588", {"start": v(-2.57, 0.1) * mm, "end": v(-2.58, 0.04) * mm});
            skLineSegment(sketch, "E589", {"start": v(-2.58, 0.04) * mm, "end": v(-2.59, -0.04) * mm});
            skLineSegment(sketch, "E590", {"start": v(-2.59, -0.04) * mm, "end": v(-2.59, -0.1) * mm});
            skLineSegment(sketch, "E591", {"start": v(-2.59, -0.1) * mm, "end": v(-2.58, -0.18) * mm});
            skLineSegment(sketch, "E592", {"start": v(-2.58, -0.18) * mm, "end": v(-2.56, -0.24) * mm});
            skLineSegment(sketch, "E593", {"start": v(-2.56, -0.24) * mm, "end": v(-2.53, -0.3) * mm});
            skLineSegment(sketch, "E594", {"start": v(-2.53, -0.3) * mm, "end": v(-2.49, -0.35) * mm});
            skLineSegment(sketch, "E595", {"start": v(-2.49, -0.35) * mm, "end": v(-2.44, -0.39) * mm});
            skLineSegment(sketch, "E596", {"start": v(-2.44, -0.39) * mm, "end": v(-2.29, -0.4) * mm});
            skLineSegment(sketch, "E597", {"start": v(-2.29, -0.4) * mm, "end": v(-2.15, -0.4) * mm});
            skLineSegment(sketch, "E598", {"start": v(-2.15, -0.4) * mm, "end": v(-2.04, -0.38) * mm});
            skLineSegment(sketch, "E599", {"start": v(-2.04, -0.38) * mm, "end": v(-1.94, -0.36) * mm});
            skLineSegment(sketch, "E600", {"start": v(-1.94, -0.36) * mm, "end": v(-1.87, -0.32) * mm});
            skLineSegment(sketch, "E601", {"start": v(-1.87, -0.32) * mm, "end": v(-1.81, -0.27) * mm});
            skLineSegment(sketch, "E602", {"start": v(-1.81, -0.27) * mm, "end": v(-1.77, -0.21) * mm});
            skLineSegment(sketch, "E603", {"start": v(-1.77, -0.21) * mm, "end": v(-1.75, -0.15) * mm});
            skLineSegment(sketch, "E604", {"start": v(-1.75, -0.15) * mm, "end": v(-1.75, -0.08) * mm});
            skLineSegment(sketch, "E605", {"start": v(-1.75, -0.08) * mm, "end": v(-1.77, 0) * mm});
            skLineSegment(sketch, "E606", {"start": v(-1.77, 0) * mm, "end": v(-1.8, 0.07) * mm});
            skLineSegment(sketch, "E607", {"start": v(-1.8, 0.07) * mm, "end": v(-1.85, 0.15) * mm});
            skLineSegment(sketch, "E608", {"start": v(-1.85, 0.15) * mm, "end": v(-1.92, 0.23) * mm});
            skLineSegment(sketch, "E609", {"start": v(-1.92, 0.23) * mm, "end": v(-2, 0.31) * mm});
            skLineSegment(sketch, "E610", {"start": v(-2, 0.31) * mm, "end": v(-2.1, 0.4) * mm});
            skLineSegment(sketch, "E611", {"start": v(-2.1, 0.4) * mm, "end": v(-2.22, 0.47) * mm});
            skLineSegment(sketch, "E612", {"start": v(0.25, 0.85) * mm, "end": v(0.2, 0.87) * mm});
            skLineSegment(sketch, "E613", {"start": v(0.2, 0.87) * mm, "end": v(0.16, 0.87) * mm});
            skLineSegment(sketch, "E614", {"start": v(0.16, 0.87) * mm, "end": v(0.1, 0.86) * mm});
            skLineSegment(sketch, "E615", {"start": v(0.1, 0.86) * mm, "end": v(0.02, 0.84) * mm});
            skLineSegment(sketch, "E616", {"start": v(0.02, 0.84) * mm, "end": v(-0.13, 0.77) * mm});
            skLineSegment(sketch, "E617", {"start": v(-0.13, 0.77) * mm, "end": v(-0.3, 0.68) * mm});
            skLineSegment(sketch, "E618", {"start": v(-0.3, 0.68) * mm, "end": v(-0.45, 0.57) * mm});
            skLineSegment(sketch, "E619", {"start": v(-0.45, 0.57) * mm, "end": v(-0.59, 0.45) * mm});
            skLineSegment(sketch, "E620", {"start": v(-0.59, 0.45) * mm, "end": v(-0.64, 0.39) * mm});
            skLineSegment(sketch, "E621", {"start": v(-0.64, 0.39) * mm, "end": v(-0.68, 0.33) * mm});
            skLineSegment(sketch, "E622", {"start": v(-0.68, 0.33) * mm, "end": v(-0.7, 0.28) * mm});
            skLineSegment(sketch, "E623", {"start": v(-0.7, 0.28) * mm, "end": v(-0.72, 0.23) * mm});
            skLineSegment(sketch, "E624", {"start": v(-0.72, 0.23) * mm, "end": v(-0.62, 0.17) * mm});
            skLineSegment(sketch, "E625", {"start": v(-0.62, 0.17) * mm, "end": v(-0.53, 0.13) * mm});
            skLineSegment(sketch, "E626", {"start": v(-0.53, 0.13) * mm, "end": v(-0.44, 0.1) * mm});
            skLineSegment(sketch, "E627", {"start": v(-0.44, 0.1) * mm, "end": v(-0.35, 0.1) * mm});
            skLineSegment(sketch, "E628", {"start": v(-0.35, 0.1) * mm, "end": v(-0.28, 0.1) * mm});
            skLineSegment(sketch, "E629", {"start": v(-0.28, 0.1) * mm, "end": v(-0.2, 0.12) * mm});
            skLineSegment(sketch, "E630", {"start": v(-0.2, 0.12) * mm, "end": v(-0.14, 0.15) * mm});
            skLineSegment(sketch, "E631", {"start": v(-0.14, 0.15) * mm, "end": v(-0.08, 0.2) * mm});
            skLineSegment(sketch, "E632", {"start": v(-0.08, 0.2) * mm, "end": v(-0.02, 0.24) * mm});
            skLineSegment(sketch, "E633", {"start": v(-0.02, 0.24) * mm, "end": v(0.03, 0.3) * mm});
            skLineSegment(sketch, "E634", {"start": v(0.03, 0.3) * mm, "end": v(0.08, 0.38) * mm});
            skLineSegment(sketch, "E635", {"start": v(0.08, 0.38) * mm, "end": v(0.12, 0.46) * mm});
            skLineSegment(sketch, "E636", {"start": v(0.12, 0.46) * mm, "end": v(0.2, 0.65) * mm});
            skLineSegment(sketch, "E637", {"start": v(0.2, 0.65) * mm, "end": v(0.25, 0.85) * mm});
            skSolve(sketch);
        }
        {
            var Q0;
            Q0=makeQuery(id+"F12.imprint","IMPRINT",FACE,{"disambiguationData":[TD([[makeQuery(id+"F12.imprint","IMPRINT",EDGE,{"derivedFrom":sQuery(id+"F12.wireOp",EDGE,"E18")}),-1.0]])]});
            extrude(context, id + "F13", {"entities" : qUnion([Q0]), "depth" : 25 * mm});
        }
    });
